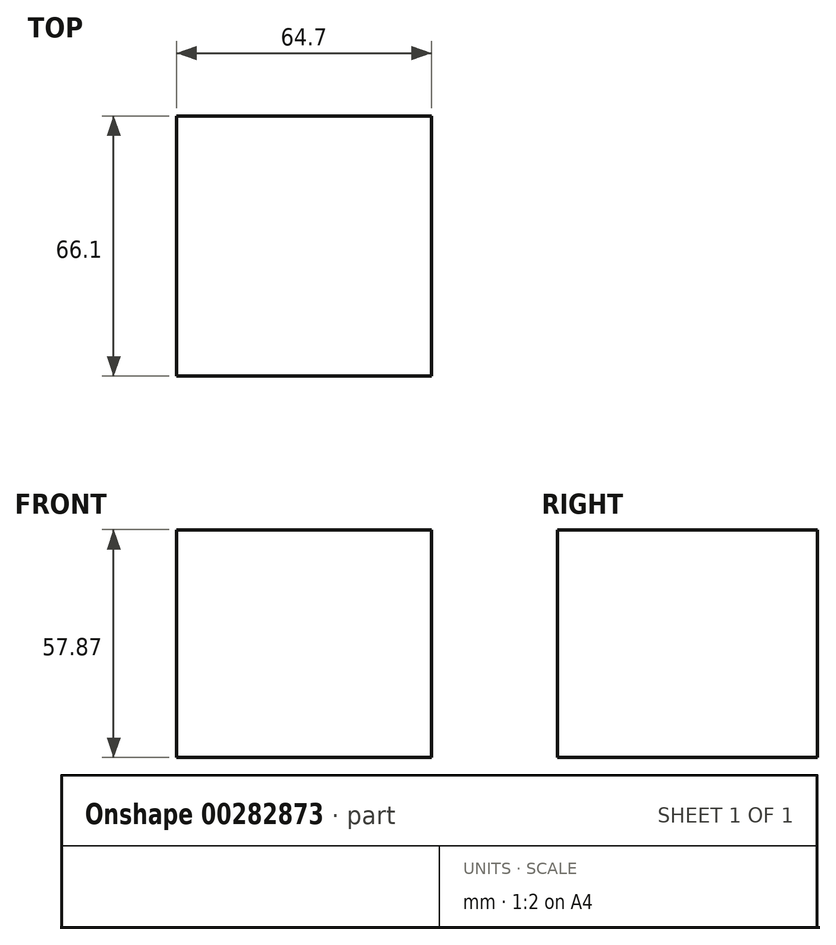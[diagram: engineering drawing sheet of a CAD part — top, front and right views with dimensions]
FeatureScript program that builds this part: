
annotation { "Feature Type Name" : "Feature", "Feature Type Description" : "" }
export const myFeature = defineFeature(function(context is Context, id is Id, definition is map)
    precondition{}
    {
        {
            var Q0;
            Q0=qCreatedBy(makeId("Right.planeOp"),FACE);
            var sketch = newSketch(context, id + "F0", { "sketchPlane" : qUnion([Q0])});
            skLineSegment(sketch, "E0.bottom", {"start": v(-34.02, 52.65) * mm, "end": v(-100.12, 52.65) * mm});
            skLineSegment(sketch, "E0.top", {"start": v(-34.02, -5.22) * mm, "end": v(-100.12, -5.22) * mm});
            skLineSegment(sketch, "E0.left", {"start": v(-34.02, 52.65) * mm, "end": v(-34.02, -5.22) * mm});
            skLineSegment(sketch, "E0.right", {"start": v(-100.12, 52.65) * mm, "end": v(-100.12, -5.22) * mm});
            skSolve(sketch);
        }
        {
            var Q0;
            Q0 = qSketchRegion(id + "F0", true);
            extrude(context, id + "F1", {"entities" : qUnion([Q0]), "depth" : 64.7 * mm});
        }
    });
